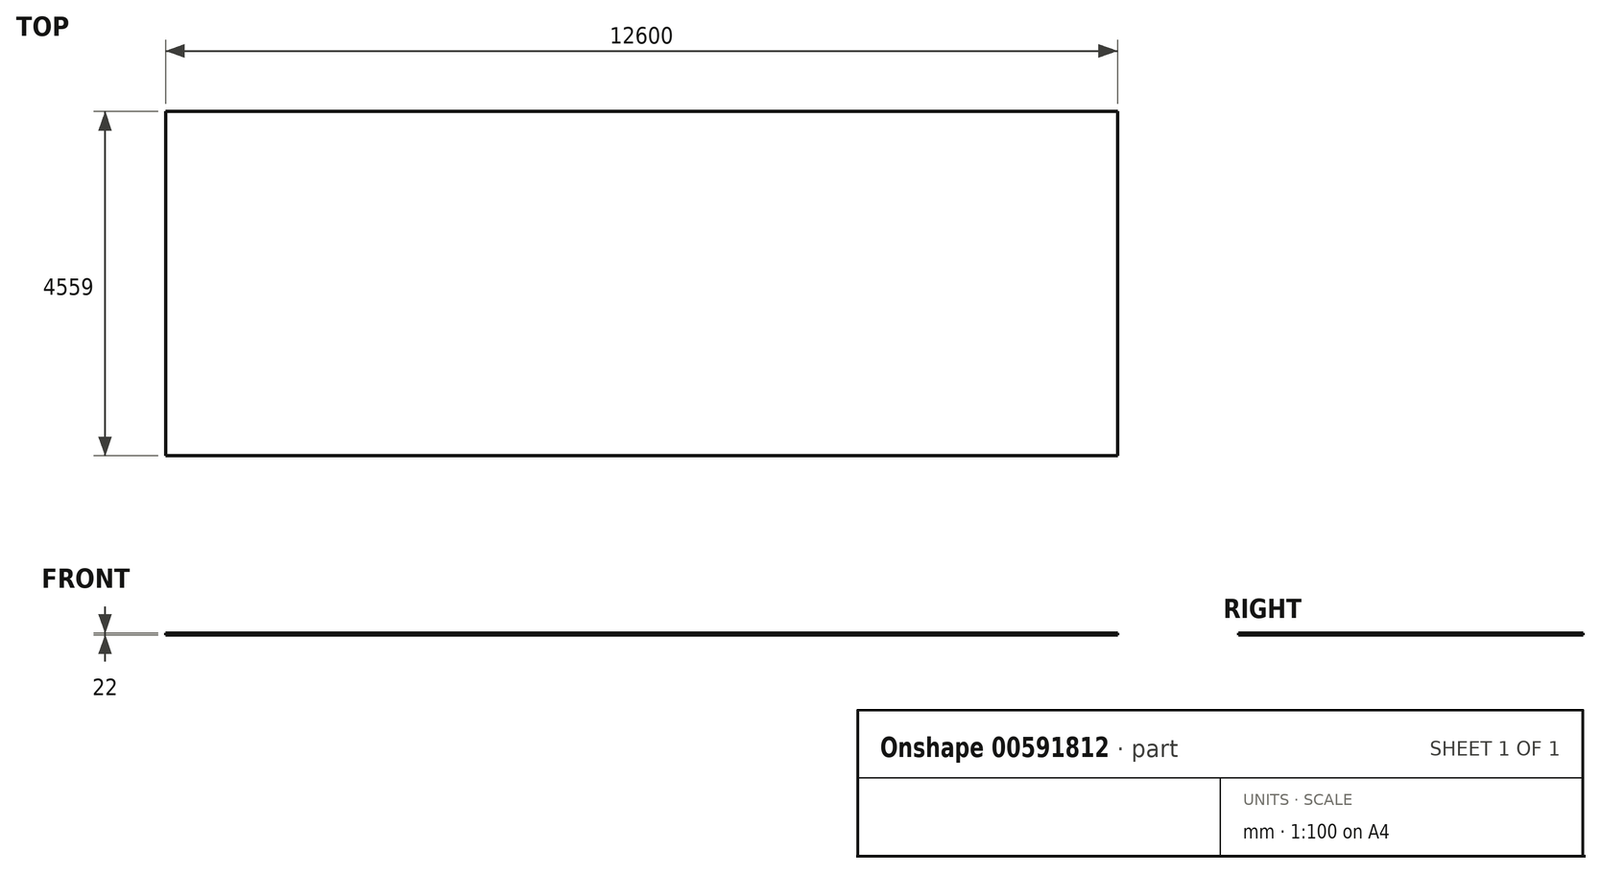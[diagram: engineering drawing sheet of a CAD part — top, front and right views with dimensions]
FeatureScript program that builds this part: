
annotation { "Feature Type Name" : "Feature", "Feature Type Description" : "" }
export const myFeature = defineFeature(function(context is Context, id is Id, definition is map)
    precondition{}
    {
        {
            var Q0;
            Q0=qCreatedBy(makeId("Top.planeOp"),FACE);
            var sketch = newSketch(context, id + "F0", { "sketchPlane" : qUnion([Q0])});
            skLineSegment(sketch, "E0.bottom", {"start": v(0, 0) * mm, "end": v(-12600, 0) * mm});
            skLineSegment(sketch, "E0.top", {"start": v(0, -4559) * mm, "end": v(-12600, -4559) * mm});
            skLineSegment(sketch, "E0.left", {"start": v(0, 0) * mm, "end": v(0, -4559) * mm});
            skLineSegment(sketch, "E0.right", {"start": v(-12600, 0) * mm, "end": v(-12600, -4559) * mm});
            skSolve(sketch);
        }
        {
            var Q0;
            Q0=makeQuery(id+"F0.imprint","IMPRINT",FACE,{"disambiguationData":[TD([[makeQuery(id+"F0.imprint","IMPRINT",EDGE,{"derivedFrom":sQuery(id+"F0.wireOp",EDGE,"E0.bottom")}),1.0]])]});
            extrude(context, id + "F1", {"entities" : qUnion([Q0]), "depth" : 22 * mm, "offsetDistance" : 25 * mm});
        }
    });
